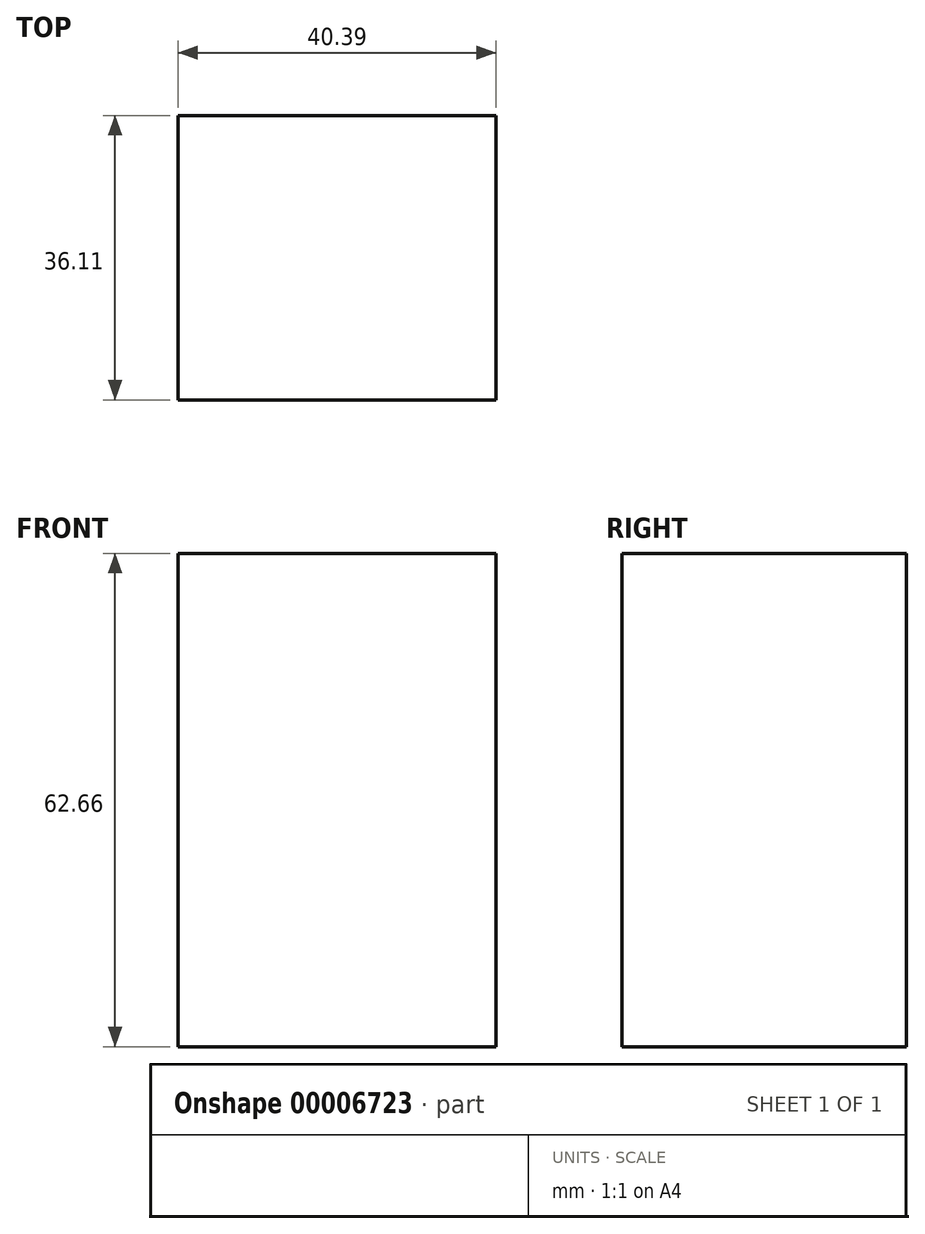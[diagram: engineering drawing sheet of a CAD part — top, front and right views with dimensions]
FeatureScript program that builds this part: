
annotation { "Feature Type Name" : "Feature", "Feature Type Description" : "" }
export const myFeature = defineFeature(function(context is Context, id is Id, definition is map)
    precondition{}
    {
        {
            var Q0;
            Q0=qCreatedBy(makeId("Front.planeOp"),FACE);
            var sketch = newSketch(context, id + "F0", { "sketchPlane" : qUnion([Q0])});
            skLineSegment(sketch, "E0.bottom", {"start": v(-13.67, 11.03) * mm, "end": v(-54.06, 11.03) * mm});
            skLineSegment(sketch, "E0.top", {"start": v(-13.67, 62.62) * mm, "end": v(-54.06, 62.62) * mm});
            skLineSegment(sketch, "E0.left", {"start": v(-13.67, 11.03) * mm, "end": v(-13.67, 62.62) * mm});
            skLineSegment(sketch, "E0.right", {"start": v(-54.06, 11.03) * mm, "end": v(-54.06, 62.62) * mm});
            skSolve(sketch);
        }
        {
            var Q0;
            Q0=makeQuery(id+"F0.imprint","IMPRINT",FACE,{"disambiguationData":[TD([[makeQuery(id+"F0.imprint","IMPRINT",EDGE,{"derivedFrom":sQuery(id+"F0.wireOp",EDGE,"E0.bottom")}),-1.0]])]});
            extrude(context, id + "F1", {"entities" : qUnion([Q0]), "oppositeDirection" : true, "depth" : 36.1 * mm});
        }
        {
            var Q0;
            Q0=makeQuery(id+"F1.opExtrude","SWEPT_FACE",FACE,{"disambiguationData":[OSD([sQuery(id+"F0.wireOp",EDGE,"E0.top")])]});
            extrude(context, id + "F2", {"entities" : qUnion([Q0]), "operationType" : NewBodyOperationType.ADD, "depth" : 11.06 * mm});
        }
    });
